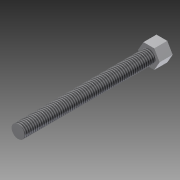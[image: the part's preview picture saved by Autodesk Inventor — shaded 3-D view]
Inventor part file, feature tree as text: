
AUTODESK INVENTOR PART (.ipt)
format: ipt  version: 2014 (Build 180170000, 170)  size: 87,040 bytes
history: native  units: mm
features: extrude x2, sketch x2, thread x1
ambient origin geometry x8: Origin, YZ Plane, XZ Plane, XY Plane, X Axis, Y Axis, Z Axis, Center Point
bodies: Solid1 (feature_tree)
feature tree (5):
  extrude  "Extrusion1"  Depth=30.0mm TaperAngle=0.0deg
  extrude  "Extrusion2"  Depth=10.0mm TaperAngle=0.0deg
  thread  "Thread1"  [1 undecoded]
  sketch  "Sketch1"  dims[d0=3.0mm d1=30.0mm d2=0.0mm]
  sketch  "Sketch2"  dims[d3=3.0mm d4=0.0mm d5=10.0mm d6=0.0mm]
note: 1 required parameter value undecoded (feature->parameter linkage not recoverable at this tier; creation-order binding heuristic only, values carry confidence <= 0.55)
